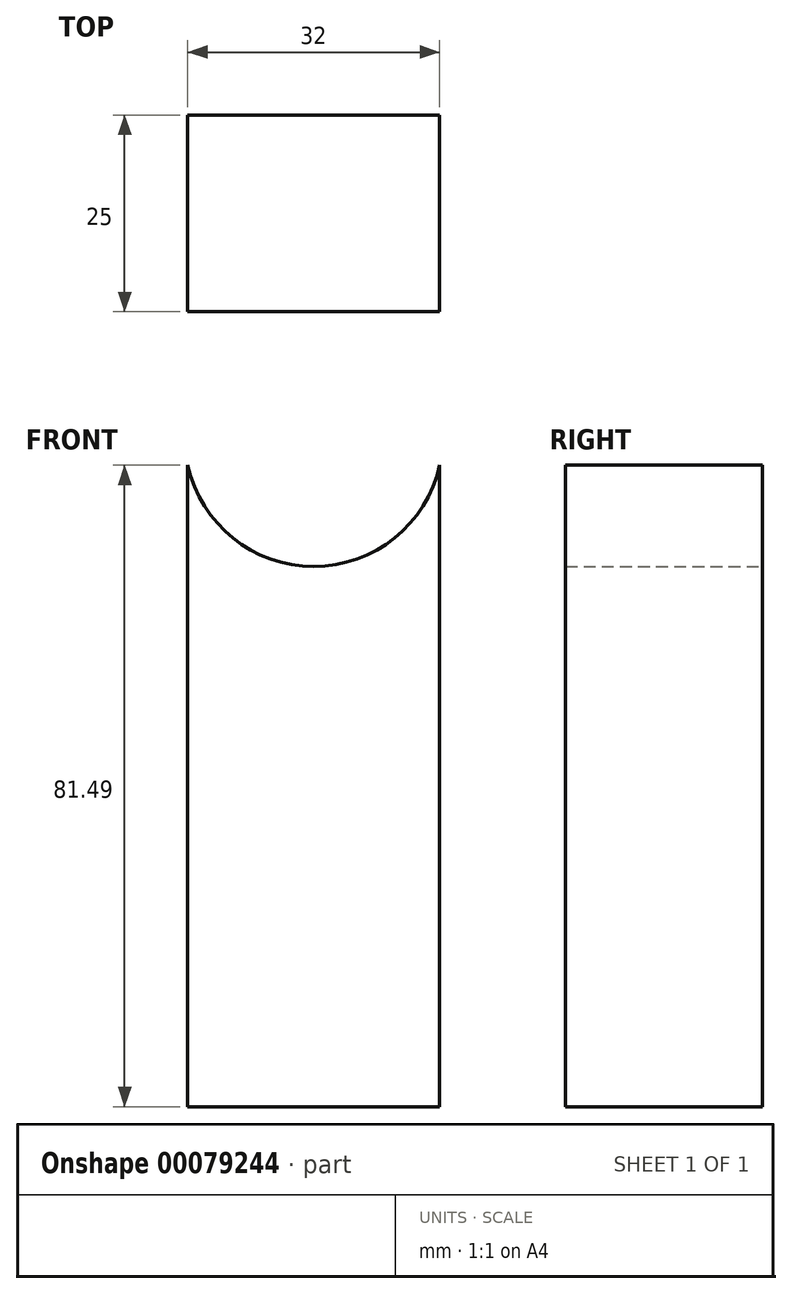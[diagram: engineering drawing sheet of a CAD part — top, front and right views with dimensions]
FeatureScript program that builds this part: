
annotation { "Feature Type Name" : "Feature", "Feature Type Description" : "" }
export const myFeature = defineFeature(function(context is Context, id is Id, definition is map)
    precondition{}
    {
        {
            var Q0;
            Q0=qCreatedBy(makeId("Front.planeOp"),FACE);
            var sketch = newSketch(context, id + "F0", { "sketchPlane" : qUnion([Q0])});
            skLineSegment(sketch, "E0.bottom", {"start": v(0, 0) * mm, "end": v(32, 0) * mm});
            skLineSegment(sketch, "E0.top", {"start": v(0, 85) * mm, "end": v(32, 85) * mm});
            skLineSegment(sketch, "E0.left", {"start": v(0, 0) * mm, "end": v(0, 85) * mm});
            skLineSegment(sketch, "E0.right", {"start": v(32, 0) * mm, "end": v(32, 85) * mm});
            skCircle(sketch, "E1", {"center": v(16, 85) * mm, "radius": 16.38 * mm});
            skSolve(sketch);
        }
        {
            var Q0;
            {var subQ0=sQuery(id+"F0.wireOp",EDGE,"E0.bottom");Q0=makeQuery(id+"F0.imprint","IMPRINT",FACE,{"disambiguationData":[TD([[makeQuery(id+"F0.imprint","IMPRINT",EDGE,{"derivedFrom":subQ0}),1.0]])]});}
            extrude(context, id + "F1", {"entities" : qUnion([Q0]), "depth" : 25 * mm});
        }
        {
            var Q0;
            {var subQ0=sQuery(id+"F0.wireOp",EDGE,"E0.bottom");Q0=makeQuery(id+"F0.imprint","IMPRINT",FACE,{"disambiguationData":[TD([[makeQuery(id+"F0.imprint","IMPRINT",EDGE,{"derivedFrom":subQ0}),1.0]])]});}
            extrude(context, id + "F2", {"entities" : qUnion([Q0]), "operationType" : NewBodyOperationType.ADD, "depth" : 5 * mm});
        }
    });
